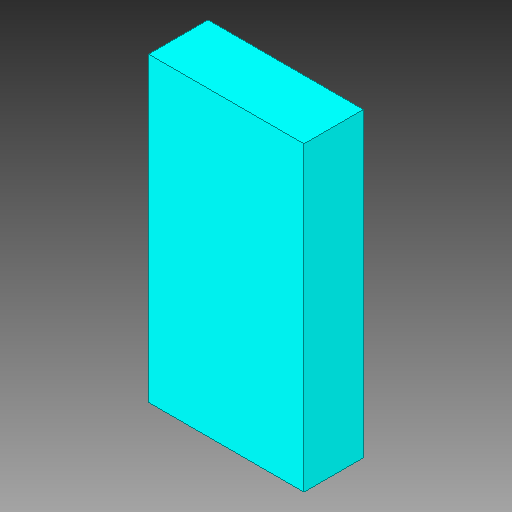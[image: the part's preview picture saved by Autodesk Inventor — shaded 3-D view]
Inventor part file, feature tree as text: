
AUTODESK INVENTOR PART (.ipt)
format: ipt  version: 2018 (Build 220112000, 112)  size: 79,360 bytes
history: native  units: in
note: dims shown in document units (in); Inventor stores cm internally (conversion verified against a paired STEP export)
features: other x1, extrude x1
ambient origin geometry x8: Origin, YZ Plane, XZ Plane, XY Plane, X Axis, Y Axis, Z Axis, Center Point
bodies: Solid1 (feature_tree)
feature tree (2):
  other  "JP1M, GND_63"
  extrude  "Extrusion1"  Depth=0.0394in TaperAngle=0.0deg
